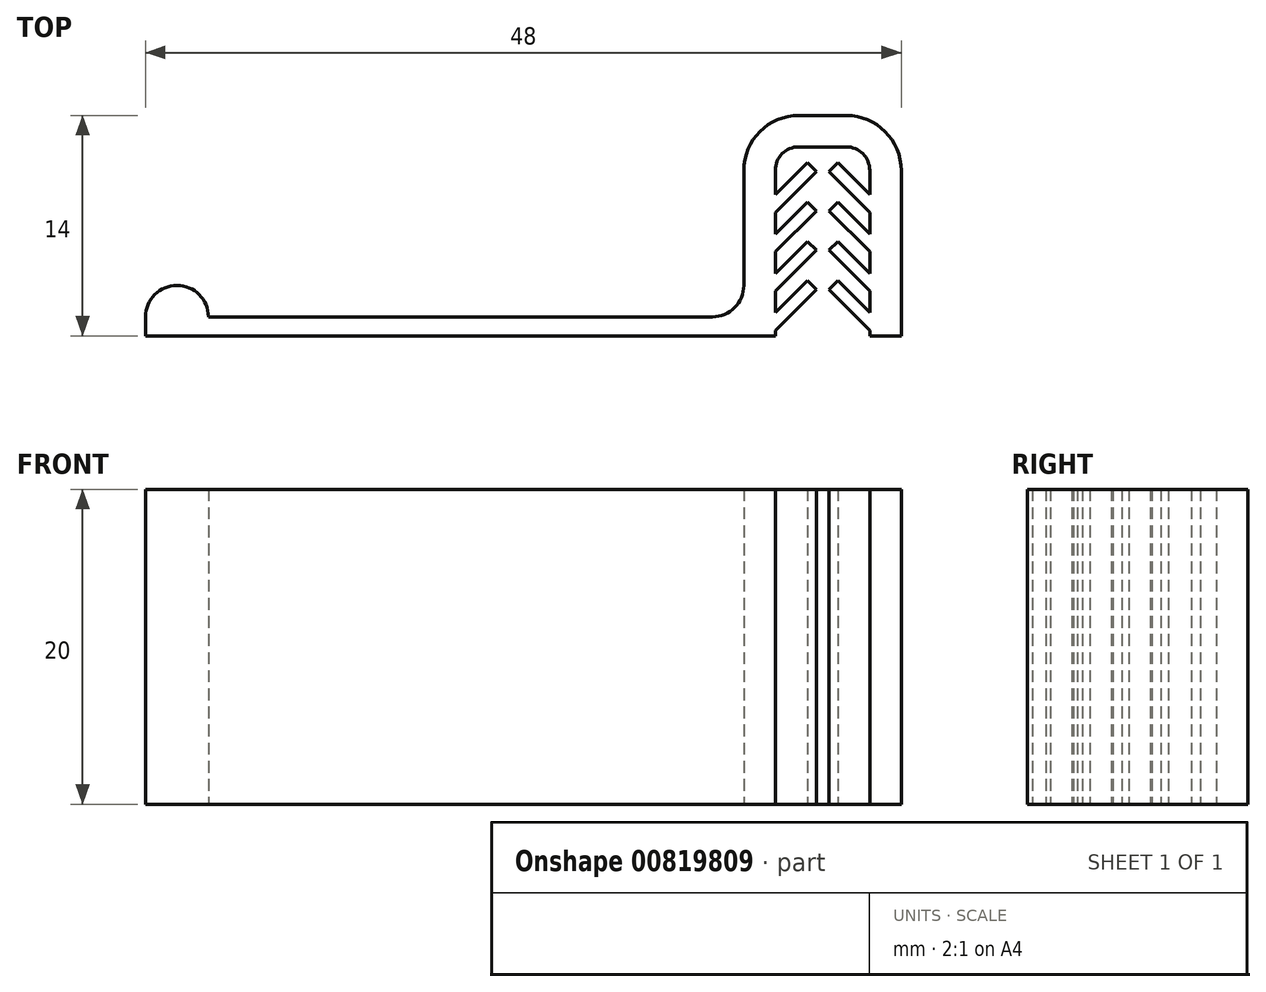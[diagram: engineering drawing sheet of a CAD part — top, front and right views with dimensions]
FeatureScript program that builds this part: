
annotation { "Feature Type Name" : "Feature", "Feature Type Description" : "" }
export const myFeature = defineFeature(function(context is Context, id is Id, definition is map)
    precondition{}
    {
        {
            var Q0;
            Q0=qCreatedBy(makeId("Top.planeOp"),FACE);
            var sketch = newSketch(context, id + "F0", { "sketchPlane" : qUnion([Q0])});
            skLineSegment(sketch, "E0", {"start": v(0, 0) * mm, "end": v(40, 0) * mm});
            skLineSegment(sketch, "E1", {"start": v(40, 0) * mm, "end": v(40, 12) * mm});
            skLineSegment(sketch, "E2", {"start": v(40, 12) * mm, "end": v(46, 12) * mm});
            skLineSegment(sketch, "E3", {"start": v(46, 12) * mm, "end": v(46, 0) * mm});
            skLineSegment(sketch, "E4.0", {"start": v(48, 14) * mm, "end": v(48, 0) * mm});
            skLineSegment(sketch, "E4.1", {"start": v(38, 14) * mm, "end": v(48, 14) * mm});
            skLineSegment(sketch, "E4.2", {"start": v(38, 1.2) * mm, "end": v(38, 14) * mm});
            skLineSegment(sketch, "E5", {"start": v(40, 8.97) * mm, "end": v(42.03, 11) * mm});
            skLineSegment(sketch, "E6", {"start": v(42.03, 11) * mm, "end": v(42.6, 10.43) * mm});
            skLineSegment(sketch, "E7", {"start": v(42.6, 10.43) * mm, "end": v(40, 7.83) * mm});
            skLineSegment(sketch, "E8", {"start": v(43, 12) * mm, "end": v(43, 0) * mm, "construction": true});
            skLineSegment(sketch, "E9.1.0.0", {"start": v(40, 6.47) * mm, "end": v(42.03, 8.5) * mm});
            skLineSegment(sketch, "E9.1.0.1", {"start": v(42.03, 8.5) * mm, "end": v(42.6, 7.93) * mm});
            skLineSegment(sketch, "E9.1.0.2", {"start": v(42.6, 7.93) * mm, "end": v(40, 5.33) * mm});
            skLineSegment(sketch, "E9.2.0.0", {"start": v(40, 3.97) * mm, "end": v(42.03, 6) * mm});
            skLineSegment(sketch, "E9.2.0.1", {"start": v(42.03, 6) * mm, "end": v(42.6, 5.43) * mm});
            skLineSegment(sketch, "E9.2.0.2", {"start": v(42.6, 5.43) * mm, "end": v(40, 2.83) * mm});
            skLineSegment(sketch, "E9.3.0.0", {"start": v(40, 1.47) * mm, "end": v(42.03, 3.5) * mm});
            skLineSegment(sketch, "E9.3.0.1", {"start": v(42.03, 3.5) * mm, "end": v(42.6, 2.93) * mm});
            skLineSegment(sketch, "E9.3.0.2", {"start": v(42.6, 2.93) * mm, "end": v(40, 0.33) * mm});
            skLineSegment(sketch, "E9.direction1", {"start": v(40, 8.97) * mm, "end": v(40, 6.47) * mm, "construction": true});
            skLineSegment(sketch, "E10.MirrorCS", {"start": v(46, 8.97) * mm, "end": v(43.97, 11) * mm});
            skLineSegment(sketch, "E11.MirrorCS", {"start": v(43.4, 2.93) * mm, "end": v(46, 0.33) * mm});
            skLineSegment(sketch, "E12.MirrorCS", {"start": v(43.97, 11) * mm, "end": v(43.4, 10.43) * mm});
            skLineSegment(sketch, "E13.MirrorCS", {"start": v(43.4, 10.43) * mm, "end": v(46, 7.83) * mm});
            skLineSegment(sketch, "E14.MirrorCS", {"start": v(46, 6.47) * mm, "end": v(43.97, 8.5) * mm});
            skLineSegment(sketch, "E15.MirrorCS", {"start": v(43.97, 8.5) * mm, "end": v(43.4, 7.93) * mm});
            skLineSegment(sketch, "E16.MirrorCS", {"start": v(43.4, 7.93) * mm, "end": v(46, 5.33) * mm});
            skLineSegment(sketch, "E17.MirrorCS", {"start": v(46, 3.97) * mm, "end": v(43.97, 6) * mm});
            skLineSegment(sketch, "E18.MirrorCS", {"start": v(43.97, 6) * mm, "end": v(43.4, 5.43) * mm});
            skLineSegment(sketch, "E19.MirrorCS", {"start": v(43.4, 5.43) * mm, "end": v(46, 2.83) * mm});
            skLineSegment(sketch, "E20.MirrorCS", {"start": v(46, 1.47) * mm, "end": v(43.97, 3.5) * mm});
            skLineSegment(sketch, "E21.MirrorCS", {"start": v(43.97, 3.5) * mm, "end": v(43.4, 2.93) * mm});
            skLineSegment(sketch, "E22", {"start": v(0, 1.2) * mm, "end": v(0, 0) * mm});
            skLineSegment(sketch, "E23", {"start": v(46, 0) * mm, "end": v(48, 0) * mm});
            skLineSegment(sketch, "E24.trimOffspring", {"start": v(4, 1.2) * mm, "end": v(38, 1.2) * mm});
            skLineSegment(sketch, "E25", {"start": v(4, 1.2) * mm, "end": v(0, 1.2) * mm, "construction": true});
            skArc(sketch, "E26", {"start": v(4, 1.2) * mm, "mid": v(2, 3.2) * mm, "end": v(0, 1.2) * mm});
            skSolve(sketch);
        }
        {
            var Q0;
            {var subQ15=sQuery(id+"F0.wireOp",EDGE,"E0");Q0=makeQuery(id+"F0.imprint","IMPRINT",FACE,{"disambiguationData":[TD([[makeQuery(id+"F0.imprint","IMPRINT",EDGE,{"derivedFrom":subQ15}),1.0]])]});}
            var Q1;
            {var subQ0=sQuery(id+"F0.wireOp",EDGE,"E9.3.0.0");Q1=makeQuery(id+"F0.imprint","IMPRINT",FACE,{"disambiguationData":[TD([[makeQuery(id+"F0.imprint","IMPRINT",EDGE,{"derivedFrom":subQ0}),-1.0]])]});}
            var Q2;
            {var subQ0=sQuery(id+"F0.wireOp",EDGE,"E9.2.0.0");Q2=makeQuery(id+"F0.imprint","IMPRINT",FACE,{"disambiguationData":[TD([[makeQuery(id+"F0.imprint","IMPRINT",EDGE,{"derivedFrom":subQ0}),-1.0]])]});}
            var Q3;
            {var subQ0=sQuery(id+"F0.wireOp",EDGE,"E9.1.0.0");Q3=makeQuery(id+"F0.imprint","IMPRINT",FACE,{"disambiguationData":[TD([[makeQuery(id+"F0.imprint","IMPRINT",EDGE,{"derivedFrom":subQ0}),-1.0]])]});}
            var Q4;
            {var subQ0=sQuery(id+"F0.wireOp",EDGE,"E5");Q4=makeQuery(id+"F0.imprint","IMPRINT",FACE,{"disambiguationData":[TD([[makeQuery(id+"F0.imprint","IMPRINT",EDGE,{"derivedFrom":subQ0}),-1.0]])]});}
            var Q5;
            {var subQ0=sQuery(id+"F0.wireOp",EDGE,"E10.MirrorCS");Q5=makeQuery(id+"F0.imprint","IMPRINT",FACE,{"disambiguationData":[TD([[makeQuery(id+"F0.imprint","IMPRINT",EDGE,{"derivedFrom":subQ0}),1.0]])]});}
            var Q6;
            {var subQ0=sQuery(id+"F0.wireOp",EDGE,"E14.MirrorCS");Q6=makeQuery(id+"F0.imprint","IMPRINT",FACE,{"disambiguationData":[TD([[makeQuery(id+"F0.imprint","IMPRINT",EDGE,{"derivedFrom":subQ0}),1.0]])]});}
            var Q7;
            {var subQ0=sQuery(id+"F0.wireOp",EDGE,"E17.MirrorCS");Q7=makeQuery(id+"F0.imprint","IMPRINT",FACE,{"disambiguationData":[TD([[makeQuery(id+"F0.imprint","IMPRINT",EDGE,{"derivedFrom":subQ0}),1.0]])]});}
            var Q8;
            {var subQ0=sQuery(id+"F0.wireOp",EDGE,"E11.MirrorCS");Q8=makeQuery(id+"F0.imprint","IMPRINT",FACE,{"disambiguationData":[TD([[makeQuery(id+"F0.imprint","IMPRINT",EDGE,{"derivedFrom":subQ0}),1.0]])]});}
            extrude(context, id + "F1", {"entities" : qUnion([Q0, Q1, Q2, Q3, Q4, Q5, Q6, Q7, Q8]), "depth" : 20 * mm, "offsetDistance" : 25 * mm});
        }
        {
            var Q0;
            Q0=makeQuery(id+"F1.opExtrude","SWEPT_EDGE",EDGE,{"disambiguationData":[OSD([sQuery(id+"F0.wireOp",EDGE,"E1"),sQuery(id+"F0.wireOp",EDGE,"E2")])]});
            var Q1;
            Q1=makeQuery(id+"F1.opExtrude","SWEPT_EDGE",EDGE,{"disambiguationData":[OSD([sQuery(id+"F0.wireOp",EDGE,"E2"),sQuery(id+"F0.wireOp",EDGE,"E3")])]});
            fillet(context, id + "F2", {"entities" : qUnion([Q0, Q1]), "radius" : 1.5 * mm, "tangentPropagation" : true, "allowEdgeOverflow" : false});
        }
        {
            var Q0;
            Q0=makeQuery(id+"F1.opExtrude","SWEPT_EDGE",EDGE,{"disambiguationData":[OSD([sQuery(id+"F0.wireOp",EDGE,"E4.1"),sQuery(id+"F0.wireOp",EDGE,"E4.2")])]});
            var Q1;
            Q1=makeQuery(id+"F1.opExtrude","SWEPT_EDGE",EDGE,{"disambiguationData":[OSD([sQuery(id+"F0.wireOp",EDGE,"E4.0"),sQuery(id+"F0.wireOp",EDGE,"E4.1")])]});
            fillet(context, id + "F3", {"entities" : qUnion([Q0, Q1]), "radius" : 3.5 * mm, "tangentPropagation" : true, "allowEdgeOverflow" : false});
        }
        {
            var Q0;
            Q0=makeQuery(id+"F1.opExtrude","SWEPT_EDGE",EDGE,{"disambiguationData":[OSD([sQuery(id+"F0.wireOp",EDGE,"E4.2"),sQuery(id+"F0.wireOp",EDGE,"E24.trimOffspring")])]});
            fillet(context, id + "F4", {"entities" : qUnion([Q0]), "radius" : 2 * mm, "tangentPropagation" : true, "allowEdgeOverflow" : false});
        }
    });
